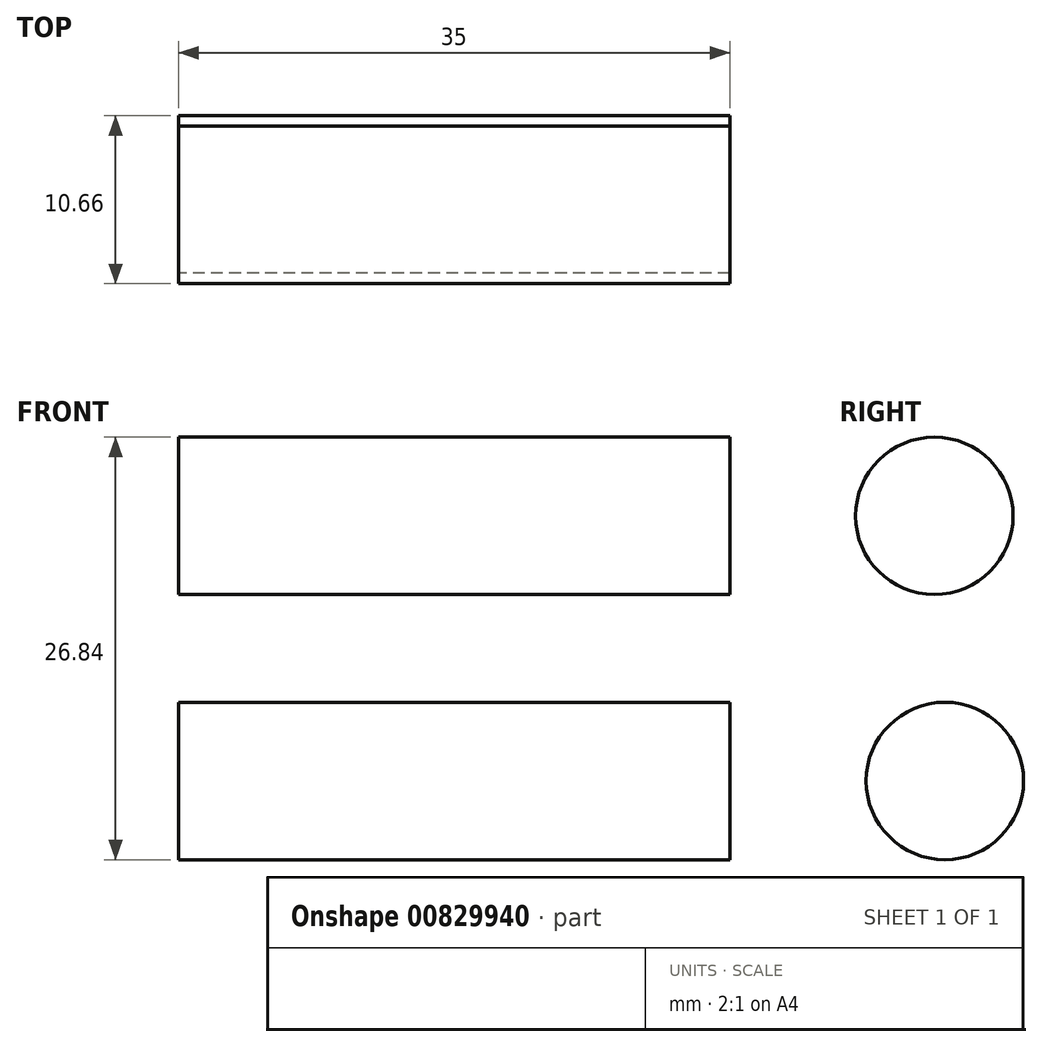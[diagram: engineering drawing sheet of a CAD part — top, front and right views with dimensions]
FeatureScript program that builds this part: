
annotation { "Feature Type Name" : "Feature", "Feature Type Description" : "" }
export const myFeature = defineFeature(function(context is Context, id is Id, definition is map)
    precondition{}
    {
        {
            var Q0;
            Q0=qCreatedBy(makeId("Right.planeOp"),FACE);
            var sketch = newSketch(context, id + "F0", { "sketchPlane" : qUnion([Q0])});
            skCircle(sketch, "E0", {"center": v(-59.17, 50.2) * mm, "radius": 5 * mm});
            skSolve(sketch);
        }
        {
            var Q0;
            Q0 = qSketchRegion(id + "F0", true);
            extrude(context, id + "F1", {"entities" : qUnion([Q0]), "depth" : 35 * mm, "offsetDistance" : 25 * mm});
        }
        {
            var Q0;
            Q0=qCreatedBy(makeId("Right.planeOp"),FACE);
            var sketch = newSketch(context, id + "F2", { "sketchPlane" : qUnion([Q0])});
            skCircle(sketch, "E1", {"center": v(-58.5, 33.37) * mm, "radius": 5 * mm});
            skSolve(sketch);
        }
        {
            var Q0;
            Q0 = qSketchRegion(id + "F2", true);
            extrude(context, id + "F3", {"entities" : qUnion([Q0]), "depth" : 35 * mm, "offsetDistance" : 25 * mm});
        }
    });
